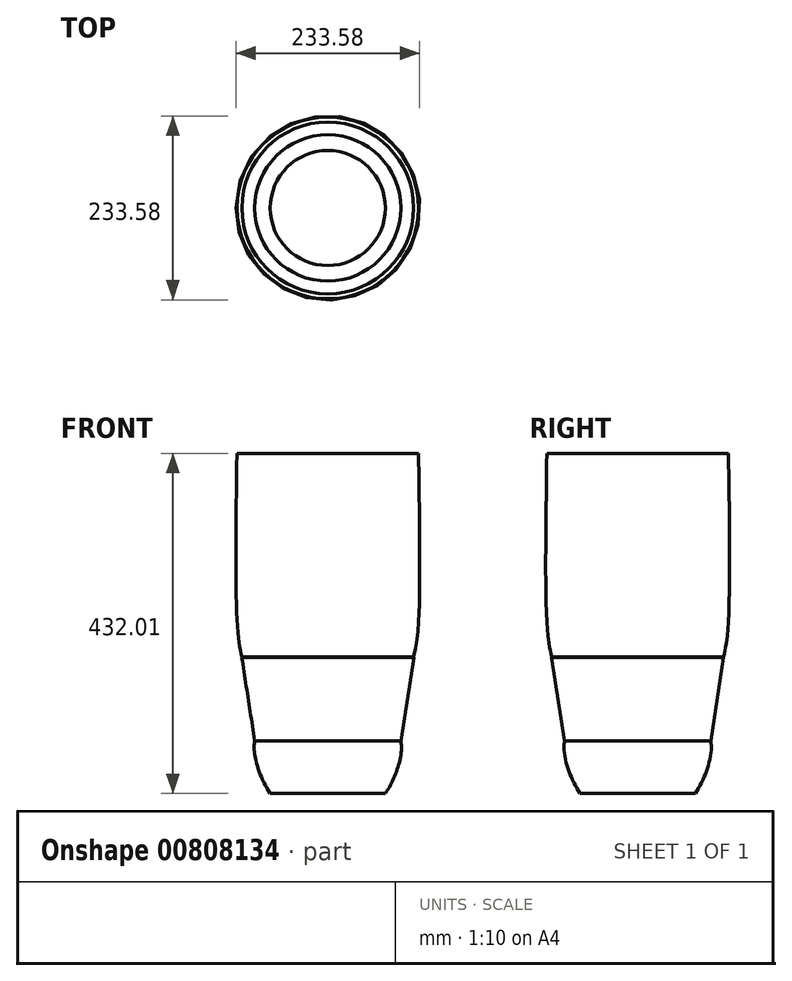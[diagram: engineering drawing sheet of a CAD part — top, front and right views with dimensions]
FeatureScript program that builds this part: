
annotation { "Feature Type Name" : "Feature", "Feature Type Description" : "" }
export const myFeature = defineFeature(function(context is Context, id is Id, definition is map)
    precondition{}
    {
        {
            var Q0;
            Q0=qCreatedBy(makeId("Front.planeOp"),FACE);
            var sketch = newSketch(context, id + "F0", { "sketchPlane" : qUnion([Q0])});
            skLineSegment(sketch, "E0", {"start": v(-109.27, 173.12) * mm, "end": v(-92.92, 67.1) * mm});
            skFitSpline(sketch, "E1", {"points": [v(-92.92, 67.1) * mm, v(-92.92, 49.31) * mm, v(-73.13, 0) * mm], "startDerivative": vector(-5.72, -43.14) * mm, "endDerivative": vector(50.08, -71.71) * mm});
            skLineSegment(sketch, "E2", {"start": v(-73.13, 0) * mm, "end": v(0, 0) * mm});
            skLineSegment(sketch, "E3", {"start": v(0, 0) * mm, "end": v(0, 0) * mm});
            skSolve(sketch);
        }
        {
            var Q0;
            Q0=qCreatedBy(makeId("Front.planeOp"),FACE);
            var sketch = newSketch(context, id + "F1", { "sketchPlane" : qUnion([Q0])});
            skLineSegment(sketch, "E4", {"start": v(0, 253.94) * mm, "end": v(0, -122.08) * mm});
            skSolve(sketch);
        }
        {
            var Q0;
            Q0=qCreatedBy(makeId("Front.planeOp"),FACE);
            var sketch = newSketch(context, id + "F2", { "sketchPlane" : qUnion([Q0])});
            skFitSpline(sketch, "E5", {"points": [v(-109.1, 173.23) * mm, v(-114.68, 208.83) * mm, v(-115.34, 432.01) * mm], "startDerivative": vector(-22.13, 97.17) * mm, "endDerivative": vector(5.7, 380.16) * mm});
            skSolve(sketch);
        }
        {
            var Q0;
            Q0=qCreatedBy(makeId("Front.planeOp"),FACE);
            var sketch = newSketch(context, id + "F3", { "sketchPlane" : qUnion([Q0])});
            skSolve(sketch);
        }
        {
            var Q0;
            Q0 = qSketchRegion(id + "F3", true);
            var Q1;
            Q1=sQuery(id+"F2.wireOp",EDGE,"E5");
            var Q2;
            Q2=sQuery(id+"F0.wireOp",EDGE,"E0");
            var Q3;
            Q3=sQuery(id+"F0.wireOp",EDGE,"E1");
            var Q4;
            Q4=sQuery(id+"F0.wireOp",EDGE,"E2");
            var Q5;
            Q5=sQuery(id+"F1.wireOp",EDGE,"E4");
            revolve(context, id + "F4", {"bodyType" : ToolBodyType.SURFACE, "surfaceOperationType" : NewSurfaceOperationType.NEW, "entities" : qUnion([Q0]), "surfaceEntities" : qUnion([Q1, Q2, Q3, Q4]), "axis" : qUnion([Q5]), "revolveType" : RevolveType.FULL});
        }
    });
